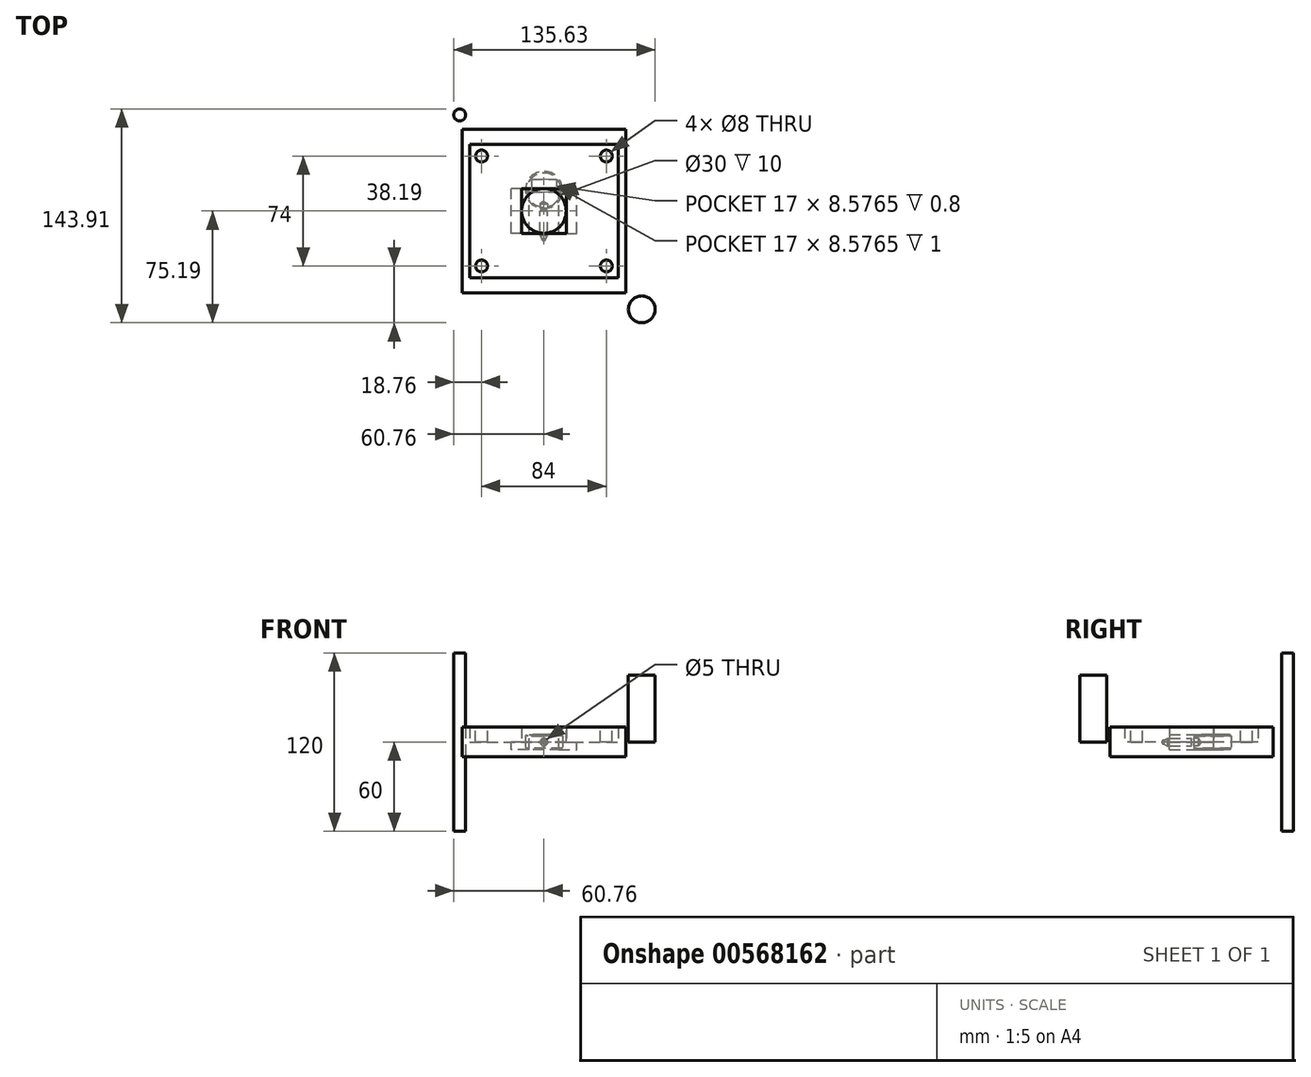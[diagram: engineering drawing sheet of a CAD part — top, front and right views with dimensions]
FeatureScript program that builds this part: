
annotation { "Feature Type Name" : "Feature", "Feature Type Description" : "" }
export const myFeature = defineFeature(function(context is Context, id is Id, definition is map)
    precondition{}
    {
        {
            var Q0;
            Q0=qCreatedBy(makeId("Top.planeOp"),FACE);
            var sketch = newSketch(context, id + "F0", { "sketchPlane" : qUnion([Q0])});
            skLineSegment(sketch, "E0.bottom", {"start": v(-50, 45) * mm, "end": v(50, 45) * mm});
            skLineSegment(sketch, "E0.top", {"start": v(-50, -45) * mm, "end": v(50, -45) * mm});
            skLineSegment(sketch, "E0.left", {"start": v(-50, 45) * mm, "end": v(-50, -45) * mm});
            skLineSegment(sketch, "E0.right", {"start": v(50, 45) * mm, "end": v(50, -45) * mm});
            skSolve(sketch);
        }
        {
            var Q0;
            Q0=makeQuery(id+"F0.imprint","IMPRINT",FACE,{"disambiguationData":[TD([[makeQuery(id+"F0.imprint","IMPRINT",EDGE,{"derivedFrom":sQuery(id+"F0.wireOp",EDGE,"E0.bottom")}),-1.0]])]});
            extrude(context, id + "F1", {"entities" : qUnion([Q0]), "depth" : 10 * mm, "offsetDistance" : 25 * mm});
        }
        {
            var Q0;
            Q0=makeQuery(id+"F1.opExtrude","CAP_FACE",FACE,{"disambiguationData":[OSD([sQuery(id+"F0.wireOp",EDGE,"E0.bottom"),sQuery(id+"F0.wireOp",EDGE,"E0.top"),sQuery(id+"F0.wireOp",EDGE,"E0.left"),sQuery(id+"F0.wireOp",EDGE,"E0.right")])],"isStart":false});
            var sketch = newSketch(context, id + "F2", { "sketchPlane" : qUnion([Q0])});
            skPoint(sketch, "E1", {"position": v(-42, 37) * mm});
            skPoint(sketch, "E2.0.1.0", {"position": v(-42, -37) * mm});
            skPoint(sketch, "E2.1.0.0", {"position": v(42, 37) * mm});
            skPoint(sketch, "E2.1.1.0", {"position": v(42, -37) * mm});
            skLineSegment(sketch, "E2.direction1", {"start": v(-42, 37) * mm, "end": v(42, 37) * mm, "construction": true});
            skLineSegment(sketch, "E2.direction2", {"start": v(-42, 37) * mm, "end": v(-42, -37) * mm, "construction": true});
            skSolve(sketch);
        }
        {
            var Q0;
            Q0=sQuery(id+"F2.wireOp",VERTEX,"E1");
            var Q1;
            Q1=sQuery(id+"F2.wireOp",VERTEX,"E2.1.0.0");
            var Q2;
            Q2=sQuery(id+"F2.wireOp",VERTEX,"E2.1.1.0");
            var Q3;
            Q3=sQuery(id+"F2.wireOp",VERTEX,"E2.0.1.0");
            var Q4;
            Q4=makeQuery(id+"F1.opExtrude","SWEPT_BODY",BODY,{"disambiguationData":[OSD([sQuery(id+"F0.wireOp",EDGE,"E0.bottom"),sQuery(id+"F0.wireOp",EDGE,"E0.top"),sQuery(id+"F0.wireOp",EDGE,"E0.left"),sQuery(id+"F0.wireOp",EDGE,"E0.right")])]});
            hole(context, id + "F3", {"style" : HoleStyle.SIMPLE, "endStyle" : HoleEndStyle.THROUGH, "holeDiameter" : 8 * mm, "isTappedThrough" : true, "tappedDepth" : 12 * mm, "tapClearance" : 3, "startFromSketch" : true, "locations" : qUnion([Q0, Q1, Q2, Q3]), "scope" : qUnion([Q4])});
        }
        {
            var Q0;
            Q0=qCreatedBy(makeId("Top.planeOp"),FACE);
            var sketch = newSketch(context, id + "F4", { "sketchPlane" : qUnion([Q0])});
            skCircle(sketch, "E3", {"center": v(65.87, -66.19) * mm, "radius": 9 * mm});
            skSolve(sketch);
        }
        {
            var Q0;
            Q0=makeQuery(id+"F4.imprint","IMPRINT",FACE,{"disambiguationData":[TD([[makeQuery(id+"F4.imprint","IMPRINT",EDGE,{"derivedFrom":sQuery(id+"F4.wireOp",EDGE,"E3")}),1.0]])]});
            var Q1;
            Q1=sQuery(id+"F4.wireOp",EDGE,"E3");
            extrude(context, id + "F5", {"entities" : qUnion([Q0]), "surfaceEntities" : qUnion([Q1]), "depth" : 45 * mm, "offsetDistance" : 25 * mm});
        }
        {
            var Q0;
            Q0=qCreatedBy(makeId("Top.planeOp"),FACE);
            var sketch = newSketch(context, id + "F6", { "sketchPlane" : qUnion([Q0])});
            skCircle(sketch, "E4", {"center": v(-56.76, 64.72) * mm, "radius": 4 * mm});
            skSolve(sketch);
        }
        {
            var Q0;
            Q0=makeQuery(id+"F6.imprint","IMPRINT",FACE,{"disambiguationData":[TD([[makeQuery(id+"F6.imprint","IMPRINT",EDGE,{"derivedFrom":sQuery(id+"F6.wireOp",EDGE,"E4")}),1.0]])]});
            extrude(context, id + "F7", {"entities" : qUnion([Q0]), "depth" : 60 * mm, "offsetDistance" : 25 * mm, "hasSecondDirection" : true, "secondDirectionOppositeDirection" : true, "secondDirectionDepth" : 60 * mm});
        }
        {
            var Q0;
            Q0=qCreatedBy(makeId("Top.planeOp"),FACE);
            var sketch = newSketch(context, id + "F8", { "sketchPlane" : qUnion([Q0])});
            skLineSegment(sketch, "E5.bottom", {"start": v(-55, 55) * mm, "end": v(55, 55) * mm});
            skLineSegment(sketch, "E5.top", {"start": v(-55, -55) * mm, "end": v(55, -55) * mm});
            skLineSegment(sketch, "E5.left", {"start": v(-55, 55) * mm, "end": v(-55, -55) * mm});
            skLineSegment(sketch, "E5.right", {"start": v(55, 55) * mm, "end": v(55, -55) * mm});
            skSolve(sketch);
        }
        {
            var Q0;
            Q0=makeQuery(id+"F8.imprint","IMPRINT",FACE,{"disambiguationData":[TD([[makeQuery(id+"F8.imprint","IMPRINT",EDGE,{"derivedFrom":sQuery(id+"F8.wireOp",EDGE,"E5.bottom")}),-1.0]])]});
            extrude(context, id + "F9", {"entities" : qUnion([Q0]), "depth" : 10 * mm, "offsetDistance" : 25 * mm, "hasSecondDirection" : true, "secondDirectionOppositeDirection" : true, "secondDirectionDepth" : 10 * mm});
        }
        {
            var Q0;
            Q0=makeQuery(id+"F1.opExtrude","CAP_FACE",FACE,{"disambiguationData":[OSD([sQuery(id+"F0.wireOp",EDGE,"E0.bottom"),sQuery(id+"F0.wireOp",EDGE,"E0.top"),sQuery(id+"F0.wireOp",EDGE,"E0.left"),sQuery(id+"F0.wireOp",EDGE,"E0.right")])],"isStart":false});
            var sketch = newSketch(context, id + "F10", { "sketchPlane" : qUnion([Q0])});
            skPoint(sketch, "E6", {"position": v(0, 0) * mm});
            skSolve(sketch);
        }
        {
            var Q0;
            Q0=sQuery(id+"F10.wireOp",VERTEX,"E6");
            var Q1;
            Q1=makeQuery(id+"F1.opExtrude","SWEPT_BODY",BODY,{"disambiguationData":[OSD([sQuery(id+"F0.wireOp",EDGE,"E0.bottom"),sQuery(id+"F0.wireOp",EDGE,"E0.top"),sQuery(id+"F0.wireOp",EDGE,"E0.left"),sQuery(id+"F0.wireOp",EDGE,"E0.right")])]});
            hole(context, id + "F11", {"style" : HoleStyle.SIMPLE, "endStyle" : HoleEndStyle.THROUGH, "holeDiameter" : 30 * mm, "isTappedThrough" : true, "tappedDepth" : 12 * mm, "tapClearance" : 3, "startFromSketch" : true, "locations" : qUnion([Q0]), "scope" : qUnion([Q1])});
        }
        {
            var Q0;
            Q0=qCreatedBy(makeId("Top.planeOp"),FACE);
            var sketch = newSketch(context, id + "F12", { "sketchPlane" : qUnion([Q0])});
            skCircle(sketch, "E7", {"center": v(0, 14.16) * mm, "radius": 12.5 * mm});
            skSolve(sketch);
        }
        {
            var Q0;
            Q0=makeQuery(id+"F12.imprint","IMPRINT",FACE,{"disambiguationData":[TD([[makeQuery(id+"F12.imprint","IMPRINT",EDGE,{"derivedFrom":sQuery(id+"F12.wireOp",EDGE,"E7")}),1.0]])]});
            extrude(context, id + "F13", {"entities" : qUnion([Q0]), "depth" : 5 * mm, "offsetDistance" : 25 * mm, "hasSecondDirection" : true, "secondDirectionOppositeDirection" : true, "secondDirectionDepth" : 5 * mm});
        }
        {
            var Q0;
            Q0=qCreatedBy(makeId("Front.planeOp"),FACE);
            var sketch = newSketch(context, id + "F14", { "sketchPlane" : qUnion([Q0])});
            skCircle(sketch, "E8", {"center": v(0, 0) * mm, "radius": 2.5 * mm});
            skSolve(sketch);
        }
        {
            var Q0;
            Q0=makeQuery(id+"F14.imprint","IMPRINT",FACE,{"disambiguationData":[TD([[makeQuery(id+"F14.imprint","IMPRINT",EDGE,{"derivedFrom":sQuery(id+"F14.wireOp",EDGE,"E8")}),1.0]])]});
            extrude(context, id + "F15", {"entities" : qUnion([Q0]), "depth" : 15 * mm, "offsetDistance" : 25 * mm});
        }
        {
            var Q0;
            Q0=qCreatedBy(makeId("Top.planeOp"),FACE);
            var sketch = newSketch(context, id + "F16", { "sketchPlane" : qUnion([Q0])});
            skLineSegment(sketch, "E9.bottom", {"start": v(-2.4, -15.43) * mm, "end": v(0, -15.43) * mm});
            skLineSegment(sketch, "E9.top", {"start": v(-2.4, -16.28) * mm, "end": v(0, -16.28) * mm});
            skLineSegment(sketch, "E9.left", {"start": v(-2.4, -15.43) * mm, "end": v(-2.4, -16.28) * mm});
            skLineSegment(sketch, "E10", {"start": v(-2.4, -16.28) * mm, "end": v(-1.25, -18.68) * mm});
            skLineSegment(sketch, "E11", {"start": v(-1.25, -18.68) * mm, "end": v(0, -18.68) * mm});
            skArc(sketch, "E12", {"start": v(-1.25, -18.68) * mm, "mid": v(-0.88, -19.57) * mm, "end": v(0, -19.93) * mm});
            skLineSegment(sketch, "E13", {"start": v(0, -15.43) * mm, "end": v(0, -19.93) * mm});
            skPoint(sketch, "E14.start.orphan", {"position": v(1.25, -18.68) * mm});
            skSolve(sketch);
        }
        {
            var Q0;
            {var subQ0=sQuery(id+"F16.wireOp",EDGE,"E9.bottom");Q0=makeQuery(id+"F16.imprint","IMPRINT",FACE,{"disambiguationData":[TD([[makeQuery(id+"F16.imprint","IMPRINT",EDGE,{"derivedFrom":subQ0}),-1.0]])]});}
            var Q1;
            {var subQ0=sQuery(id+"F16.wireOp",EDGE,"E9.top");Q1=makeQuery(id+"F16.imprint","IMPRINT",FACE,{"disambiguationData":[TD([[makeQuery(id+"F16.imprint","IMPRINT",EDGE,{"derivedFrom":subQ0}),-1.0]])]});}
            var Q2;
            {var subQ0=sQuery(id+"F16.wireOp",EDGE,"E11");Q2=makeQuery(id+"F16.imprint","IMPRINT",FACE,{"disambiguationData":[TD([[makeQuery(id+"F16.imprint","IMPRINT",EDGE,{"derivedFrom":subQ0}),-1.0]])]});}
            var Q3;
            Q3=sQuery(id+"F16.wireOp",EDGE,"E13");
            revolve(context, id + "F17", {"entities" : qUnion([Q0, Q1, Q2]), "axis" : qUnion([Q3]), "revolveType" : RevolveType.FULL});
        }
        {
            var Q0;
            Q0=makeQuery(id+"F13.opExtrude","CAP_FACE",FACE,{"disambiguationData":[OSD([sQuery(id+"F12.wireOp",EDGE,"E7")])],"isStart":false});
            var sketch = newSketch(context, id + "F18", { "sketchPlane" : qUnion([Q0])});
            skLineSegment(sketch, "E15.bottom", {"start": v(-8.5, 21.36) * mm, "end": v(8.5, 21.36) * mm});
            skLineSegment(sketch, "E15.top", {"start": v(-8.5, 12.78) * mm, "end": v(8.5, 12.78) * mm});
            skLineSegment(sketch, "E15.left", {"start": v(-8.5, 21.36) * mm, "end": v(-8.5, 12.78) * mm});
            skLineSegment(sketch, "E15.right", {"start": v(8.5, 21.36) * mm, "end": v(8.5, 12.78) * mm});
            skCircle(sketch, "E16", {"center": v(-5, 7.51) * mm, "radius": 1.35 * mm});
            skCircle(sketch, "E17", {"center": v(5, 7.51) * mm, "radius": 1.35 * mm});
            skSolve(sketch);
        }
        {
            var Q0;
            Q0=makeQuery(id+"F18.imprint","IMPRINT",FACE,{"disambiguationData":[TD([[makeQuery(id+"F18.imprint","IMPRINT",EDGE,{"derivedFrom":sQuery(id+"F18.wireOp",EDGE,"E15.bottom")}),-1.0]])]});
            extrude(context, id + "F19", {"entities" : qUnion([Q0]), "operationType" : NewBodyOperationType.REMOVE, "oppositeDirection" : true, "depth" : 1 * mm, "offsetDistance" : 25 * mm});
        }
        {
            var Q0;
            Q0=makeQuery(id+"F13.opExtrude","CAP_EDGE",EDGE,{"disambiguationData":[OSD([sQuery(id+"F12.wireOp",EDGE,"E7")])],"isStart":true});
            var Q1;
            Q1=makeQuery(id+"F13.opExtrude","CAP_EDGE",EDGE,{"disambiguationData":[OSD([sQuery(id+"F12.wireOp",EDGE,"E7")])],"isStart":false});
            chamfer(context, id + "F20", {"entities" : qUnion([Q0, Q1]), "width" : 1 * mm, "tangentPropagation" : true});
        }
        {
            var Q0;
            Q0=makeQuery(id+"F19.boolean.opBoolean","COPY",EDGE,{"derivedFrom":makeQuery(id+"F19.opExtrude","CAP_EDGE",EDGE,{"disambiguationData":[OSD([sQuery(id+"F18.wireOp",EDGE,"E15.bottom")])],"isStart":true})});
            var Q1;
            Q1=makeQuery(id+"F19.boolean.opBoolean","COPY",EDGE,{"derivedFrom":makeQuery(id+"F19.opExtrude","CAP_EDGE",EDGE,{"disambiguationData":[OSD([sQuery(id+"F18.wireOp",EDGE,"E15.right")])],"isStart":true})});
            var Q2;
            Q2=makeQuery(id+"F19.boolean.opBoolean","COPY",EDGE,{"derivedFrom":makeQuery(id+"F19.opExtrude","CAP_EDGE",EDGE,{"disambiguationData":[OSD([sQuery(id+"F18.wireOp",EDGE,"E15.top")])],"isStart":true})});
            var Q3;
            Q3=makeQuery(id+"F19.boolean.opBoolean","COPY",EDGE,{"derivedFrom":makeQuery(id+"F19.opExtrude","CAP_EDGE",EDGE,{"disambiguationData":[OSD([sQuery(id+"F18.wireOp",EDGE,"E15.left")])],"isStart":true})});
            fillet(context, id + "F21", {"entities" : qUnion([Q0, Q1, Q2, Q3]), "radius" : 0.2 * mm, "tangentPropagation" : true, "allowEdgeOverflow" : false});
        }
        {
            var Q0;
            Q0=qCreatedBy(makeId("Front.planeOp"),FACE);
            var sketch = newSketch(context, id + "F22", { "sketchPlane" : qUnion([Q0])});
            skPoint(sketch, "E18", {"position": v(0, 0) * mm});
            skSolve(sketch);
        }
        {
            var Q0;
            Q0=sQuery(id+"F22.wireOp",VERTEX,"E18");
            var Q1;
            Q1=makeQuery(id+"F13.opExtrude","SWEPT_BODY",BODY,{"disambiguationData":[OSD([sQuery(id+"F12.wireOp",EDGE,"E7")])]});
            hole(context, id + "F23", {"style" : HoleStyle.SIMPLE, "endStyle" : HoleEndStyle.BLIND, "holeDiameter" : 5 * mm, "holeDepth" : 3 * mm, "isTappedThrough" : true, "tappedDepth" : 12 * mm, "tapClearance" : 3, "locations" : qUnion([Q0]), "scope" : qUnion([Q1])});
        }
        {
            var Q0;
            Q0=qCreatedBy(makeId("Front.planeOp"),FACE);
            var sketch = newSketch(context, id + "F24", { "sketchPlane" : qUnion([Q0])});
            skLineSegment(sketch, "E19.bottom", {"start": v(-15, 10) * mm, "end": v(15, 10) * mm});
            skLineSegment(sketch, "E19.top", {"start": v(-15, -5) * mm, "end": v(-10, -5) * mm});
            skLineSegment(sketch, "E19.left", {"start": v(-15, 10) * mm, "end": v(-15, 0) * mm});
            skLineSegment(sketch, "E19.right", {"start": v(15, 10) * mm, "end": v(15, 0) * mm});
            skLineSegment(sketch, "E20.top", {"start": v(-10, 5) * mm, "end": v(10, 5) * mm});
            skLineSegment(sketch, "E20.left", {"start": v(-10, -5) * mm, "end": v(-10, 5) * mm});
            skLineSegment(sketch, "E20.right", {"start": v(10, -5) * mm, "end": v(10, 5) * mm});
            skLineSegment(sketch, "E21.bottom", {"start": v(-15, -5) * mm, "end": v(-22, -5) * mm});
            skLineSegment(sketch, "E21.top", {"start": v(-15, 0) * mm, "end": v(-22, 0) * mm});
            skLineSegment(sketch, "E21.right", {"start": v(-22, -5) * mm, "end": v(-22, 0) * mm});
            skPoint(sketch, "E22.oppositeSnap0", {"position": v(-18.5, 0) * mm});
            skLineSegment(sketch, "E22.bottom", {"start": v(15, -5) * mm, "end": v(22, -5) * mm});
            skLineSegment(sketch, "E22.top", {"start": v(15, 0) * mm, "end": v(22, 0) * mm});
            skLineSegment(sketch, "E22.right", {"start": v(22, -5) * mm, "end": v(22, 0) * mm});
            skLineSegment(sketch, "E23.trimOffspring", {"start": v(10, -5) * mm, "end": v(15, -5) * mm});
            skSolve(sketch);
        }
        {
            var Q0;
            Q0=makeQuery(id+"F24.imprint","IMPRINT",FACE,{"disambiguationData":[TD([[makeQuery(id+"F24.imprint","IMPRINT",EDGE,{"derivedFrom":sQuery(id+"F24.wireOp",EDGE,"E19.bottom")}),-1.0]])]});
            extrude(context, id + "F25", {"entities" : qUnion([Q0]), "depth" : 15 * mm, "offsetDistance" : 25 * mm, "hasSecondDirection" : true, "secondDirectionOppositeDirection" : true, "secondDirectionDepth" : 15 * mm});
        }
    });
